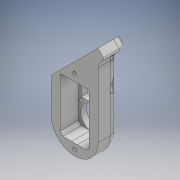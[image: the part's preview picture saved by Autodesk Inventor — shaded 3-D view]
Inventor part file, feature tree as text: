
AUTODESK INVENTOR PART (.ipt)
format: ipt  version: 2018 (Build 220112000, 112)  size: 841,728 bytes
history: native  units: mm
features: sketch x33, extrude x26, projected_geometry x23, fillet x10, hole x7, chamfer x5, other x3, mirror x1, plane x1, reference x1
ambient origin geometry x8: Origin, YZ Plane, XZ Plane, XY Plane, X Axis, Y Axis, Z Axis, Center Point
bodies: Solid1 (feature_tree)
feature tree (110):
  extrude  "Extrusion1"  Depth=45.0mm
  extrude  "Extrusion2"  Depth=1.95mm
  hole  "Hole1"  [1 undecoded]
  hole  "Hole2"  [1 undecoded]
  fillet  "Fillet1"  Radius=14.0mm
  extrude  "Extrusion3"  Depth=18.5mm
  extrude  "Extrusion4"  Depth=20.5mm
  extrude  "Extrusion5"  Depth=2.195mm
  extrude  "Extrusion6"  Depth=20.5mm
  hole  "Hole3"  [1 undecoded]
  extrude  "Extrusion7"  Depth=0.5mm
  extrude  "Extrusion8"  Depth=5.0mm TaperAngle=0.0deg
  extrude  "Extrusion9"  Depth=24.5mm
  extrude  "Extrusion10"  Depth=10.0mm
  extrude  "Extrusion11"  Depth=14.5mm
  extrude  "Extrusion12"  Depth=14.5mm
  extrude  "Extrusion13"  Depth=5.0mm
  extrude  "Extrusion14"  Depth=2.25mm
  extrude  "Extrusion15"  Depth=5.0mm
  extrude  "Extrusion16"  Depth=9.0mm
  extrude  "Extrusion17"  Depth=4.0mm
  chamfer  "Chamfer1"  Distance=1.0mm
  fillet  "Fillet7"  Radius=20.7mm
  fillet  "Fillet8"  Radius=32.0mm
  mirror  "Mirror1"
  extrude  "Extrusion18"  Depth=1.0mm TaperAngle=0.0deg
  extrude  "Extrusion19"  Depth=8.0mm
  extrude  "Extrusion20"  Depth=0.2mm TaperAngle=0.0deg
  extrude  "Extrusion21"  Depth=0.5mm TaperAngle=0.0deg
  extrude  "Extrusion22"  Depth=5.0mm TaperAngle=0.0deg
  extrude  "Extrusion23"  Depth=0.2mm TaperAngle=0.0deg
  chamfer  "Chamfer3"  Distance=0.2mm
  chamfer  "Chamfer4"  Distance=2.5mm Angle=45.0deg
  fillet  "Fillet12"  Radius=1.5mm
  fillet  "Fillet15"  Radius=0.5mm
  hole  "Hole6"  [1 undecoded]
  extrude  "Extrusion24"  Depth=40.0mm
  fillet  "Fillet16"  Radius=25.0mm
  fillet  "Fillet17"  Radius=25.0mm
  chamfer  "Chamfer5"  Distance=25.0mm
  hole  "Hole7"  [1 undecoded]
  extrude  "Extrusion25"  Depth=7.0mm TaperAngle=45.0deg
  fillet  "Fillet18"  Radius=4.0mm
  fillet  "Fillet19"  Radius=8.0mm
  hole  "Hole8"  [1 undecoded]
  plane  "Work Plane1"
  hole  "Hole9"  [1 undecoded]
  fillet  "Fillet20"  Radius=4.9mm
  extrude  "Extrusion26"  Depth=5.7mm
  chamfer  "Chamfer6"  Distance=11.0mm
  sketch  "Sketch1"  dims[d0=24.5mm d1=45.0mm]
  sketch  "Sketch2"  dims[d2=1.95mm d3=0.0mm d4=2.25mm]
  projected_geometry  "Projected Loop1"
  sketch  "Sketch3"  dims[d5=20.0mm d6=2.25mm]
  projected_geometry  "Projected Loop2"
  sketch  "Sketch4"  dims[d7=5.25mm d8=5.25mm d9=14.0mm]
  projected_geometry  "Projected Loop3"
  sketch  "Sketch5"  dims[d10=5.25mm d11=18.5mm]
  projected_geometry  "Projected Loop4"
  sketch  "Sketch6"  dims[d12=10.0mm d13=0.0mm d14=20.5mm]
  projected_geometry  "Projected Loop5"
  sketch  "Sketch7"  dims[d15=2.0mm d16=2.195mm]
  projected_geometry  "Projected Loop6"
  sketch  "Sketch8"  dims[d17=2.0mm]
  projected_geometry  "Projected Loop7"
  sketch  "Sketch9"  dims[d18=2.4mm d19=6.0mm d20=4.4mm d21=2.0mm d22=90.0deg d23=8.0mm d24=20.594885mm d25=20.5mm]
  projected_geometry  "Projected Loop8"
  projected_geometry  "Projected Loop9"
  sketch  "Sketch10"  dims[d26=26.65mm d27=2.0mm]
  projected_geometry  "Projected Loop10"
  projected_geometry  "Projected Loop11"
  sketch  "Sketch11"  dims[d28=2.0mm]
  projected_geometry  "Projected Loop12"
  sketch  "Sketch12"  dims[d29=2.4mm d30=6.0mm d31=4.4mm d32=2.0mm d33=90.0deg d34=8.0mm d35=20.594885mm d36=0.5mm]
  sketch  "Sketch13"  dims[d37=18.0mm d38=5.0mm d39=0.0mm]
  sketch  "Sketch14"  dims[d41=10.0mm d42=0.0mm d43=24.5mm]
  projected_geometry  "Projected Loop13"
  sketch  "Sketch15"  dims[d44=1.15mm d45=0.0mm d46=10.0mm]
  sketch  "Sketch16"  dims[d47=21.0mm d48=14.5mm]
  projected_geometry  "Projected Loop14"
  sketch  "Sketch17"  dims[d49=20.0mm d50=14.5mm]
  projected_geometry  "Projected Loop15"
  sketch  "Sketch18"  dims[d51=24.5mm d52=5.0mm]
  projected_geometry  "Projected Loop16"
  sketch  "Sketch19"  dims[d53=5.0mm d54=2.25mm]
  projected_geometry  "Projected Loop17"
  sketch  "Sketch20"  dims[d55=2.25mm d56=5.0mm]
  projected_geometry  "Projected Loop18"
  sketch  "Sketch22"  dims[d57=5.0mm d58=9.0mm]
  sketch  "Sketch26"  dims[d59=14.75mm d60=4.0mm d61=1.0mm d62=0.0mm d63=20.7mm]
  sketch  "Sketch27"  dims[d64=2.4mm d65=6.0mm d66=4.4mm d67=2.0mm d68=90.0deg d69=8.0mm d70=20.594885mm d72=32.0mm]
  projected_geometry  "Projected Loop22"
  sketch  "Sketch28"  dims[d73=5.0mm d74=0.0mm d75=1.0mm d76=0.0mm]
  sketch  "Sketch29"  dims[d77=12.25mm d78=0.0mm d80=8.0mm]
  sketch  "Sketch31"  dims[d81=4.5mm d82=0.0mm d84=0.2mm d85=0.0mm]
  projected_geometry  "Projected Loop24"
  sketch  "Sketch32"  dims[d86=21.0mm d87=0.5mm d88=0.0mm]
  reference  "Reference1"
  sketch  "Sketch33"  dims[d91=8.0mm d92=0.0mm d93=5.0mm d94=0.0mm]
  sketch  "Sketch34"  dims[d95=5.0mm d96=0.0mm d98=0.2mm d99=0.0mm d100=0.2mm d101=0.0mm d102=2.5mm d103=2.0mm d104=45.0deg d105=1.5mm d114=0.5mm]
  projected_geometry  "Projected Loop25"
  sketch  "Sketch35"  dims[d115=22.55mm d116=0.0mm d128=40.0mm]
  sketch  "Sketch36"  dims[d129=70.0mm d130=40.0mm d131=25.0mm d132=0.0mm d133=25.0mm d134=0.0mm d135=25.0mm d136=0.0mm]
  projected_geometry  "Projected Loop26"
  sketch  "Sketch37"  dims[d137=2.0mm d138=0.0mm d143=8.0mm]
  sketch  "Sketch38"  dims[d144=2.0mm d145=0.0mm d148=7.0mm d149=2.0mm d150=45.0deg d152=4.0mm d153=2.0mm d154=45.0deg d155=8.0mm d158=8.0mm d159=4.9mm d160=4.9mm d161=3.2mm d162=6.0mm d163=6.3mm d164=2.0mm d165=90.0deg d166=8.0mm d167=20.594885mm d168=5.7mm d169=11.0mm d170=0.0mm d171=0.7mm d172=1.5mm d173=2.0mm d174=2.0mm d175=45.0deg d176=6.0mm d177=3.2mm d178=7.01mm d179=6.3mm d180=2.0mm d181=90.0deg d182=10.979mm d183=20.594885mm d184=5.7mm d185=11.0mm d186=0.0mm d187=1.5mm d188=1.5mm d189=14.0mm d190=17.0mm d191=9.0mm d192=3.3mm d193=6.0mm d194=3.023mm d195=2.0mm d196=14.3117mm d197=8.0mm d198=20.594885mm d199=-100.0mm d200=5.7mm d201=6.0mm d202=3.023mm d203=2.0mm d204=14.3117mm d205=96.0mm d206=0.0mm d207=1.0mm d208=16.0mm d209=2.0mm d210=0.0mm d211=1.5mm d212=2.0mm d213=45.0deg]
  projected_geometry  "Projected Loop27"
  parser-record x1  (decoder bookkeeping rows leaked as tree rows — omitted from the tree; the rows remain in map.json)
  other  "bottomarm.iam"
  other  "arm1:1"
note: 7 required parameter values undecoded (feature->parameter linkage not recoverable at this tier; creation-order binding heuristic only, values carry confidence <= 0.55)
note: 1 file-system path scrubbed to <path> (originals preserved in map.json)
